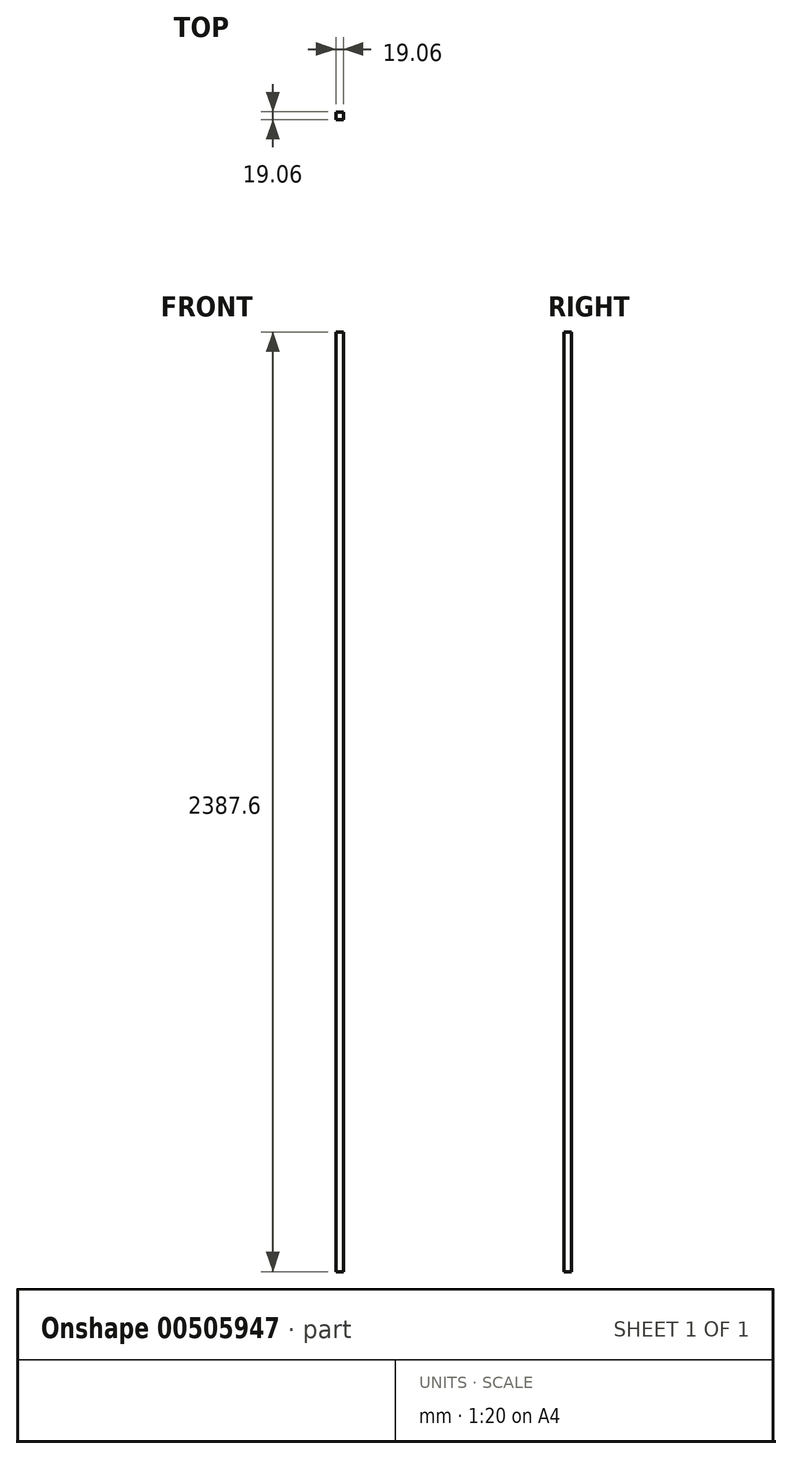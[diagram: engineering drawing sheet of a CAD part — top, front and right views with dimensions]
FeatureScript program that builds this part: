
annotation { "Feature Type Name" : "Feature", "Feature Type Description" : "" }
export const myFeature = defineFeature(function(context is Context, id is Id, definition is map)
    precondition{}
    {
        {
            var Q0;
            Q0=qCreatedBy(makeId("Top.planeOp"),FACE);
            var sketch = newSketch(context, id + "F0", { "sketchPlane" : qUnion([Q0])});
            skLineSegment(sketch, "E0.bottom", {"start": v(-9.52, 9.52) * mm, "end": v(9.53, 9.52) * mm});
            skLineSegment(sketch, "E0.top", {"start": v(-9.53, -9.53) * mm, "end": v(9.52, -9.53) * mm});
            skLineSegment(sketch, "E0.left", {"start": v(-9.52, 9.52) * mm, "end": v(-9.53, -9.53) * mm});
            skLineSegment(sketch, "E0.right", {"start": v(9.53, 9.52) * mm, "end": v(9.52, -9.53) * mm});
            skPoint(sketch, "E0.middle", {"position": v(0, 0) * mm});
            skSolve(sketch);
        }
        {
            var Q0;
            Q0 = qSketchRegion(id + "F0", true);
            extrude(context, id + "F1", {"entities" : qUnion([Q0]), "depth" : 2387.6 * mm});
        }
    });
